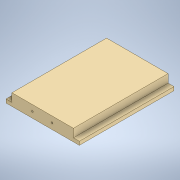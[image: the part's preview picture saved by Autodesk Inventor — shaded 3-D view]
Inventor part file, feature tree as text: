
AUTODESK INVENTOR PART (.ipt)
format: ipt  version: 2021 (Build 250183000, 183)  size: 123,904 bytes
history: native  units: in
note: dims shown in document units (in); Inventor stores cm internally (conversion verified against a paired STEP export)
features: sketch x2, extrude x1, hole x1
ambient origin geometry x8: Origin, YZ Plane, XZ Plane, XY Plane, X Axis, Y Axis, Z Axis, Center Point
bodies: Body1 (feature_tree)
feature tree (4):
  extrude  "Extrusion2"  Depth=3.1496in TaperAngle=0.0deg
  hole  "Hole1"  [1 undecoded]
  sketch  "Sketch5"  dims[d12=2.0472in d14=3.1496in d15=0.0in]
  sketch  "Sketch6"  dims[d16=0.0591in d17=0.1969in d19=0.6811in d20=0.0561in d21=0.2247in d22=0.1575in d23=0.0787in d24=90.0deg d25=0.3422in d26=0.0in d27=0.6567in d31=0.1181in d32=0.1969in d33=0.1969in d38=0.1181in d39=0.3937in d40=0.0591in d41=0.1969in]
note: 1 required parameter value undecoded (feature->parameter linkage not recoverable at this tier; creation-order binding heuristic only, values carry confidence <= 0.55)
